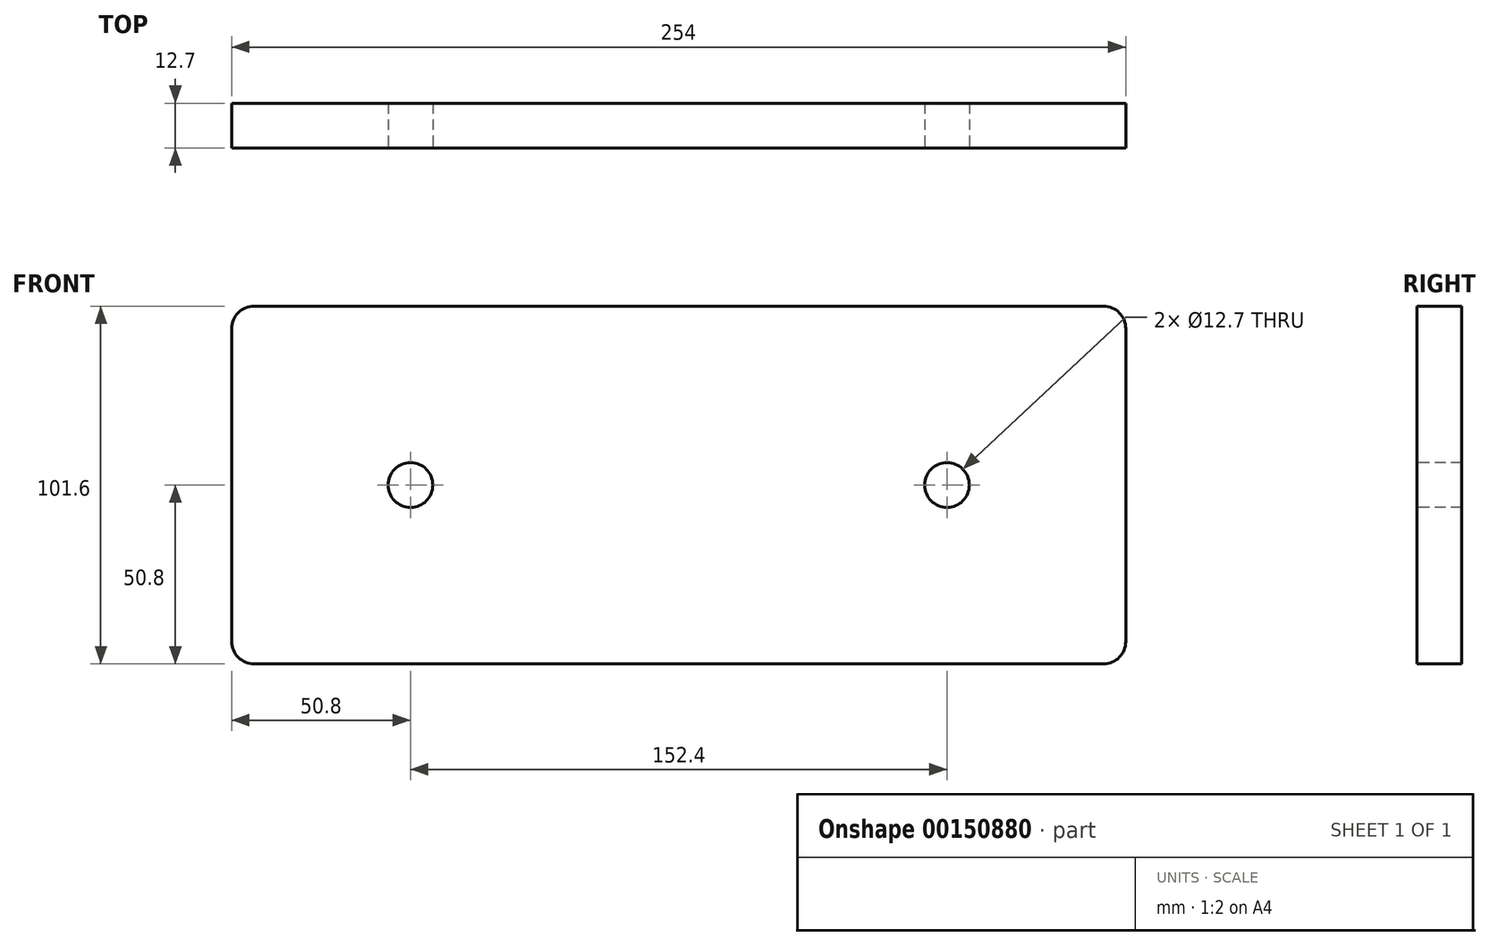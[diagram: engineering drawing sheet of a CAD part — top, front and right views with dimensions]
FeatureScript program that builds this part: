
annotation { "Feature Type Name" : "Feature", "Feature Type Description" : "" }
export const myFeature = defineFeature(function(context is Context, id is Id, definition is map)
    precondition{}
    {
        {
            var Q0;
            Q0=qCreatedBy(makeId("Front.planeOp"),FACE);
            var sketch = newSketch(context, id + "F0", { "sketchPlane" : qUnion([Q0])});
            skLineSegment(sketch, "E0.bottom", {"start": v(0, 0) * mm, "end": v(254, 0) * mm});
            skLineSegment(sketch, "E0.top", {"start": v(0, 101.6) * mm, "end": v(254, 101.6) * mm});
            skLineSegment(sketch, "E0.left", {"start": v(0, 0) * mm, "end": v(0, 101.6) * mm});
            skLineSegment(sketch, "E0.right", {"start": v(254, 0) * mm, "end": v(254, 101.6) * mm});
            skSolve(sketch);
        }
        {
            var Q0;
            Q0=makeQuery(id+"F0.imprint","IMPRINT",FACE,{"disambiguationData":[TD([[makeQuery(id+"F0.imprint","IMPRINT",EDGE,{"derivedFrom":sQuery(id+"F0.wireOp",EDGE,"E0.bottom")}),1.0]])]});
            extrude(context, id + "F1", {"entities" : qUnion([Q0]), "depth" : 12.7 * mm});
        }
        {
            var Q0;
            Q0=makeQuery(id+"F1.opExtrude","CAP_FACE",FACE,{"disambiguationData":[OSD([sQuery(id+"F0.wireOp",EDGE,"E0.bottom"),sQuery(id+"F0.wireOp",EDGE,"E0.top"),sQuery(id+"F0.wireOp",EDGE,"E0.left"),sQuery(id+"F0.wireOp",EDGE,"E0.right")])],"isStart":false});
            var sketch = newSketch(context, id + "F2", { "sketchPlane" : qUnion([Q0])});
            skPoint(sketch, "E1", {"position": v(50.8, 50.8) * mm});
            skPoint(sketch, "E2", {"position": v(203.2, 50.8) * mm});
            skSolve(sketch);
        }
        {
            var Q0;
            Q0=sQuery(id+"F2.wireOp",VERTEX,"E1");
            var Q1;
            Q1=sQuery(id+"F2.wireOp",VERTEX,"E2");
            var Q2;
            Q2=makeQuery(id+"F1.opExtrude","SWEPT_BODY",BODY,{"disambiguationData":[OSD([sQuery(id+"F0.wireOp",EDGE,"E0.bottom"),sQuery(id+"F0.wireOp",EDGE,"E0.top"),sQuery(id+"F0.wireOp",EDGE,"E0.left"),sQuery(id+"F0.wireOp",EDGE,"E0.right")])]});
            hole(context, id + "F3", {"style" : HoleStyle.SIMPLE, "endStyle" : HoleEndStyle.THROUGH, "holeDiameter" : 12.7 * mm, "locations" : qUnion([Q0, Q1]), "scope" : qUnion([Q2]), "isTappedThrough" : true});
        }
        {
            var Q0;
            Q0=makeQuery(id+"F1.opExtrude","SWEPT_EDGE",EDGE,{"disambiguationData":[OSD([sQuery(id+"F0.wireOp",EDGE,"E0.top"),sQuery(id+"F0.wireOp",EDGE,"E0.left")])]});
            var Q1;
            Q1=makeQuery(id+"F1.opExtrude","SWEPT_EDGE",EDGE,{"disambiguationData":[OSD([sQuery(id+"F0.wireOp",EDGE,"E0.bottom"),sQuery(id+"F0.wireOp",EDGE,"E0.left")])]});
            var Q2;
            Q2=makeQuery(id+"F1.opExtrude","SWEPT_EDGE",EDGE,{"disambiguationData":[OSD([sQuery(id+"F0.wireOp",EDGE,"E0.bottom"),sQuery(id+"F0.wireOp",EDGE,"E0.right")])]});
            var Q3;
            Q3=makeQuery(id+"F1.opExtrude","SWEPT_EDGE",EDGE,{"disambiguationData":[OSD([sQuery(id+"F0.wireOp",EDGE,"E0.top"),sQuery(id+"F0.wireOp",EDGE,"E0.right")])]});
            fillet(context, id + "F4", {"entities" : qUnion([Q0, Q1, Q2, Q3]), "radius" : 6.35 * mm, "tangentPropagation" : true, "allowEdgeOverflow" : false});
        }
    });
